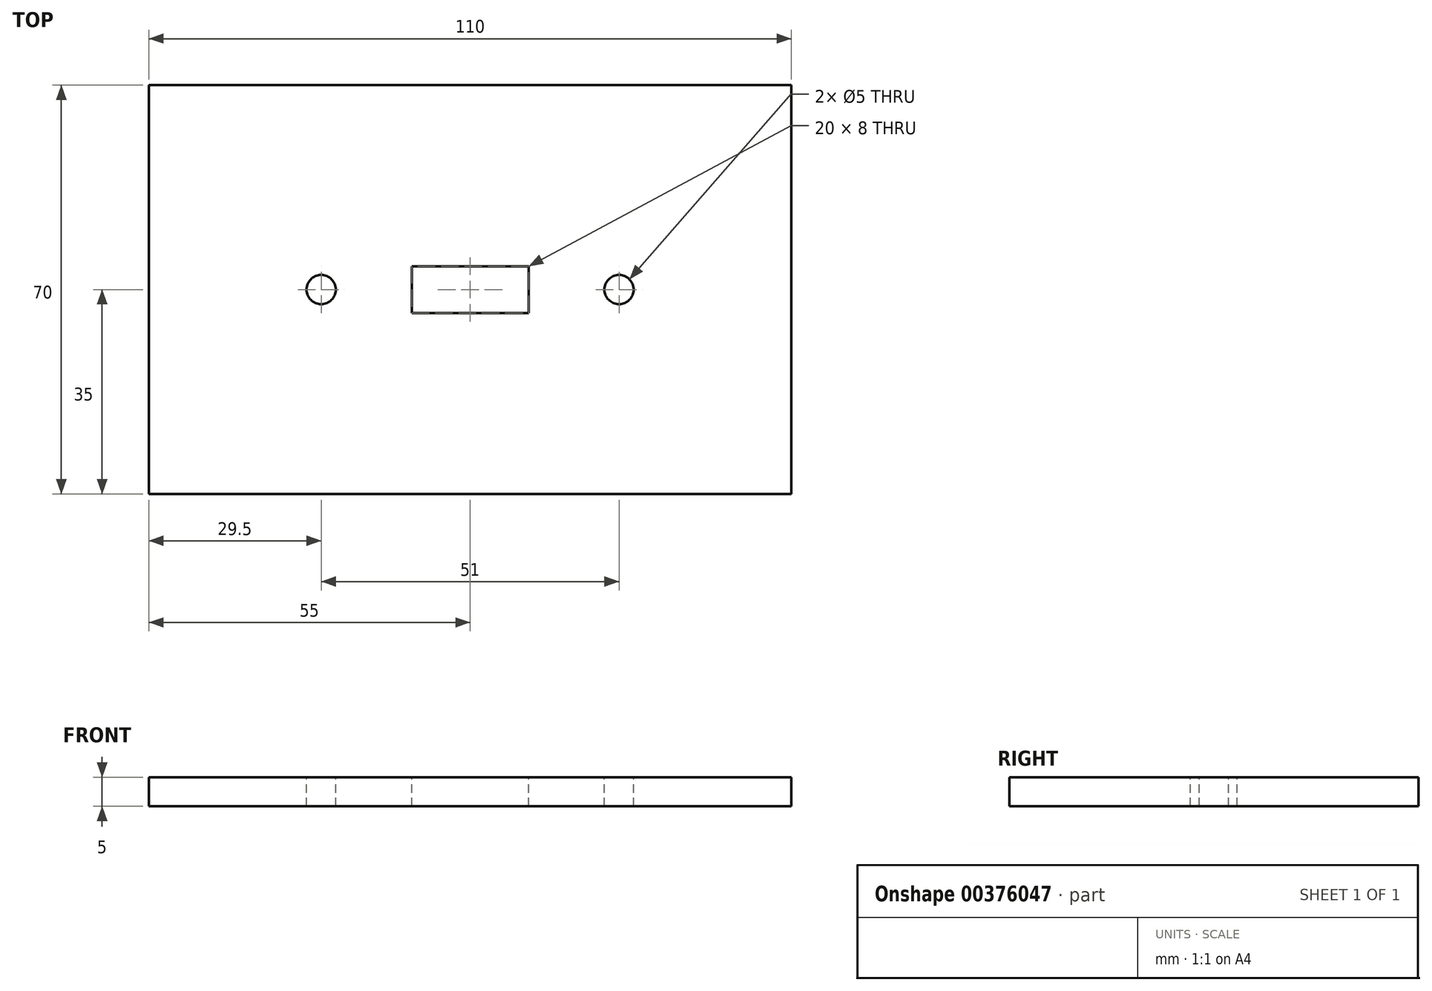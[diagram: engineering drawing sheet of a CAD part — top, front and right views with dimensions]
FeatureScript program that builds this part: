
annotation { "Feature Type Name" : "Feature", "Feature Type Description" : "" }
export const myFeature = defineFeature(function(context is Context, id is Id, definition is map)
    precondition{}
    {
        {
            var Q0;
            Q0=qCreatedBy(makeId("Top.planeOp"),FACE);
            var sketch = newSketch(context, id + "F0", { "sketchPlane" : qUnion([Q0])});
            skLineSegment(sketch, "E0.bottom", {"start": v(55, -35) * mm, "end": v(-55, -35) * mm});
            skLineSegment(sketch, "E0.top", {"start": v(55, 35) * mm, "end": v(-55, 35) * mm});
            skLineSegment(sketch, "E0.left", {"start": v(55, -35) * mm, "end": v(55, 35) * mm});
            skLineSegment(sketch, "E0.right", {"start": v(-55, -35) * mm, "end": v(-55, 35) * mm});
            skPoint(sketch, "E0.middle", {"position": v(0, 0) * mm});
            skSolve(sketch);
        }
        {
            var Q0;
            Q0 = qSketchRegion(id + "F0", true);
            extrude(context, id + "F1", {"entities" : qUnion([Q0]), "depth" : 5 * mm});
        }
        {
            var Q0;
            Q0=makeQuery(id+"F1.opExtrude","CAP_FACE",FACE,{"disambiguationData":[OSD([sQuery(id+"F0.wireOp",EDGE,"E0.bottom"),sQuery(id+"F0.wireOp",EDGE,"E0.top"),sQuery(id+"F0.wireOp",EDGE,"E0.left"),sQuery(id+"F0.wireOp",EDGE,"E0.right")])],"isStart":false});
            var sketch = newSketch(context, id + "F2", { "sketchPlane" : qUnion([Q0])});
            skLineSegment(sketch, "E1.bottom", {"start": v(10, -4) * mm, "end": v(-10, -4) * mm});
            skLineSegment(sketch, "E1.top", {"start": v(10, 4) * mm, "end": v(-10, 4) * mm});
            skLineSegment(sketch, "E1.left", {"start": v(10, -4) * mm, "end": v(10, 4) * mm});
            skLineSegment(sketch, "E1.right", {"start": v(-10, -4) * mm, "end": v(-10, 4) * mm});
            skPoint(sketch, "E1.middle", {"position": v(0, 0) * mm});
            skSolve(sketch);
        }
        {
            var Q0;
            Q0 = qSketchRegion(id + "F2", true);
            extrude(context, id + "F3", {"entities" : qUnion([Q0]), "operationType" : NewBodyOperationType.REMOVE, "endBound" : BoundingType.THROUGH_ALL, "oppositeDirection" : true, "depth" : 25.4 * mm});
        }
        {
            var Q0;
            Q0=makeQuery(id+"F1.opExtrude","CAP_FACE",FACE,{"disambiguationData":[OSD([sQuery(id+"F0.wireOp",EDGE,"E0.bottom"),sQuery(id+"F0.wireOp",EDGE,"E0.top"),sQuery(id+"F0.wireOp",EDGE,"E0.left"),sQuery(id+"F0.wireOp",EDGE,"E0.right")])],"isStart":false});
            var sketch = newSketch(context, id + "F4", { "sketchPlane" : qUnion([Q0])});
            skCircle(sketch, "E2", {"center": v(-25.5, 0) * mm, "radius": 2.5 * mm});
            skSolve(sketch);
        }
        {
            var Q0;
            Q0 = qSketchRegion(id + "F4", true);
            extrude(context, id + "F5", {"entities" : qUnion([Q0]), "operationType" : NewBodyOperationType.REMOVE, "endBound" : BoundingType.THROUGH_ALL, "oppositeDirection" : true, "depth" : 25.4 * mm});
        }
        {
            var Q0;
            Q0=makeQuery(id+"F1.opExtrude","CAP_FACE",FACE,{"disambiguationData":[OSD([sQuery(id+"F0.wireOp",EDGE,"E0.bottom"),sQuery(id+"F0.wireOp",EDGE,"E0.top"),sQuery(id+"F0.wireOp",EDGE,"E0.left"),sQuery(id+"F0.wireOp",EDGE,"E0.right")])],"isStart":false});
            var sketch = newSketch(context, id + "F6", { "sketchPlane" : qUnion([Q0])});
            skCircle(sketch, "E3", {"center": v(25.5, 0) * mm, "radius": 2.5 * mm});
            skSolve(sketch);
        }
        {
            var Q0;
            Q0=makeQuery(id+"F6.imprint","IMPRINT",FACE,{"disambiguationData":[TD([[makeQuery(id+"F6.imprint","IMPRINT",EDGE,{"derivedFrom":sQuery(id+"F6.wireOp",EDGE,"E3")}),1.0]])]});
            var Q1;
            Q1=sQuery(id+"F6.wireOp",EDGE,"E3");
            extrude(context, id + "F7", {"entities" : qUnion([Q0]), "operationType" : NewBodyOperationType.REMOVE, "surfaceEntities" : qUnion([Q1]), "endBound" : BoundingType.THROUGH_ALL, "oppositeDirection" : true, "depth" : 25.4 * mm});
        }
    });
